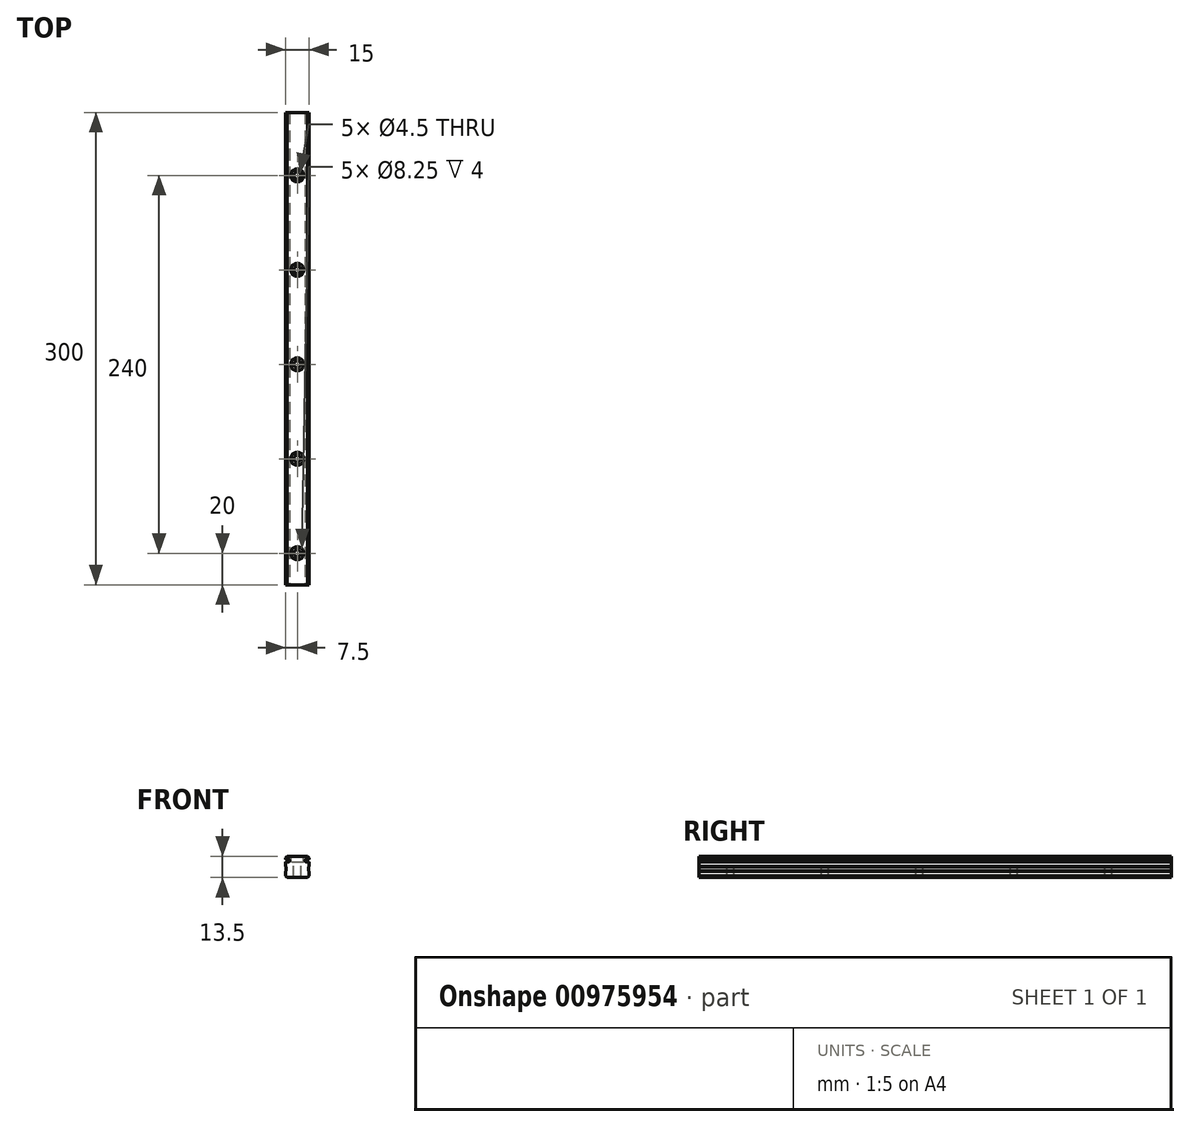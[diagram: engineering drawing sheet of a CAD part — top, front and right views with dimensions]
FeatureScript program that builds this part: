
annotation { "Feature Type Name" : "Feature", "Feature Type Description" : "" }
export const myFeature = defineFeature(function(context is Context, id is Id, definition is map)
    precondition{}
    {
        {
            var Q0;
            Q0=qCreatedBy(makeId("Front.planeOp"),FACE);
            var sketch = newSketch(context, id + "F0", { "sketchPlane" : qUnion([Q0])});
            skLineSegment(sketch, "E0.bottom", {"start": v(7.5, -6.75) * mm, "end": v(-7.5, -6.75) * mm});
            skLineSegment(sketch, "E0.top", {"start": v(7.5, 6.75) * mm, "end": v(-7.5, 6.75) * mm});
            skLineSegment(sketch, "E0.left", {"start": v(7.5, 5.25) * mm, "end": v(7.5, 6.75) * mm});
            skLineSegment(sketch, "E0.right", {"start": v(-7.5, 5.25) * mm, "end": v(-7.5, 6.75) * mm});
            skPoint(sketch, "E0.middle", {"position": v(0, 0) * mm});
            skLineSegment(sketch, "E1", {"start": v(-6.5, 6.75) * mm, "end": v(-7.5, 5.75) * mm});
            skLineSegment(sketch, "E2.MirrorCS", {"start": v(6.5, 6.75) * mm, "end": v(7.5, 5.75) * mm});
            skLineSegment(sketch, "E3.MirrorCS", {"start": v(-6.5, -6.75) * mm, "end": v(-7.5, -5.75) * mm});
            skLineSegment(sketch, "E4.MirrorCS", {"start": v(6.5, -6.75) * mm, "end": v(7.5, -5.75) * mm});
            skLineSegment(sketch, "E5", {"start": v(7.2, 0.25) * mm, "end": v(7.2, -2.75) * mm});
            skLineSegment(sketch, "E6", {"start": v(7.2, -2.75) * mm, "end": v(7.5, -2.75) * mm});
            skLineSegment(sketch, "E7", {"start": v(7.2, 0.25) * mm, "end": v(7.5, 0.25) * mm});
            skLineSegment(sketch, "E8.MirrorCS", {"start": v(-7.2, -2.75) * mm, "end": v(-7.5, -2.75) * mm});
            skLineSegment(sketch, "E9.MirrorCS", {"start": v(-7.2, 0.25) * mm, "end": v(-7.5, 0.25) * mm});
            skLineSegment(sketch, "E10.MirrorCS", {"start": v(-7.2, 0.25) * mm, "end": v(-7.2, -2.75) * mm});
            skLineSegment(sketch, "E11", {"start": v(5, 4.25) * mm, "end": v(5, 3.75) * mm});
            skLineSegment(sketch, "E12", {"start": v(5.5, 4.75) * mm, "end": v(7, 4.75) * mm});
            skLineSegment(sketch, "E13", {"start": v(5.5, 3.25) * mm, "end": v(7, 3.25) * mm});
            skLineSegment(sketch, "E14.MirrorCS", {"start": v(-5, 4.25) * mm, "end": v(-5, 3.75) * mm});
            skLineSegment(sketch, "E15.MirrorCS", {"start": v(-5.5, 4.75) * mm, "end": v(-7, 4.75) * mm});
            skLineSegment(sketch, "E16.MirrorCS", {"start": v(-5.5, 3.25) * mm, "end": v(-7, 3.25) * mm});
            skPoint(sketch, "E17.newPointA", {"position": v(7.5, 4.75) * mm});
            skArc(sketch, "E17.filletArc", {"start": v(7, 4.75) * mm, "mid": v(7.35, 4.9) * mm, "end": v(7.5, 5.25) * mm});
            skLineSegment(sketch, "E18", {"start": v(7.5, 2.75) * mm, "end": v(7.5, -6.75) * mm});
            skPoint(sketch, "E19.visualSharp", {"position": v(7.5, 3.25) * mm});
            skArc(sketch, "E19.filletArc", {"start": v(7.5, 2.75) * mm, "mid": v(7.35, 3.1) * mm, "end": v(7, 3.25) * mm});
            skPoint(sketch, "E20.newPointB", {"position": v(-7.5, 4.75) * mm});
            skArc(sketch, "E20.filletArc", {"start": v(-7.5, 5.25) * mm, "mid": v(-7.35, 4.9) * mm, "end": v(-7, 4.75) * mm});
            skLineSegment(sketch, "E21", {"start": v(-7.5, 2.75) * mm, "end": v(-7.5, -6.75) * mm});
            skPoint(sketch, "E22.visualSharp", {"position": v(-7.5, 3.25) * mm});
            skArc(sketch, "E22.filletArc", {"start": v(-7, 3.25) * mm, "mid": v(-7.35, 3.1) * mm, "end": v(-7.5, 2.75) * mm});
            skLineSegment(sketch, "E23", {"start": v(7.5, 0.25) * mm, "end": v(7.2, -0.05) * mm});
            skLineSegment(sketch, "E24", {"start": v(7.5, -2.75) * mm, "end": v(7.2, -2.45) * mm});
            skLineSegment(sketch, "E25.MirrorCS", {"start": v(-7.5, 0.25) * mm, "end": v(-7.2, -0.05) * mm});
            skLineSegment(sketch, "E26.MirrorCS", {"start": v(-7.5, -2.75) * mm, "end": v(-7.2, -2.45) * mm});
            skPoint(sketch, "E27.visualSharp", {"position": v(5, 4.75) * mm});
            skArc(sketch, "E27.filletArc", {"start": v(5.5, 4.75) * mm, "mid": v(5.15, 4.6) * mm, "end": v(5, 4.25) * mm});
            skPoint(sketch, "E28.visualSharp", {"position": v(5, 3.25) * mm});
            skArc(sketch, "E28.filletArc", {"start": v(5, 3.75) * mm, "mid": v(5.15, 3.4) * mm, "end": v(5.5, 3.25) * mm});
            skPoint(sketch, "E29.visualSharp", {"position": v(-5, 4.75) * mm});
            skArc(sketch, "E29.filletArc", {"start": v(-5, 4.25) * mm, "mid": v(-5.15, 4.6) * mm, "end": v(-5.5, 4.75) * mm});
            skPoint(sketch, "E30.visualSharp", {"position": v(-5, 3.25) * mm});
            skArc(sketch, "E30.filletArc", {"start": v(-5.5, 3.25) * mm, "mid": v(-5.15, 3.4) * mm, "end": v(-5, 3.75) * mm});
            skSolve(sketch);
        }
        {
            var Q0;
            {var subQ0=sQuery(id+"F0.wireOp",EDGE,"E1");Q0=makeQuery(id+"F0.imprint","IMPRINT",FACE,{"disambiguationData":[TD([[makeQuery(id+"F0.imprint","IMPRINT",EDGE,{"derivedFrom":subQ0}),1.0]])]});}
            var Q1;
            {var subQ0=sQuery(id+"F0.wireOp",EDGE,"E9.MirrorCS");Q1=makeQuery(id+"F0.imprint","IMPRINT",FACE,{"disambiguationData":[TD([[makeQuery(id+"F0.imprint","IMPRINT",EDGE,{"derivedFrom":subQ0}),1.0]])]});}
            var Q2;
            {var subQ0=sQuery(id+"F0.wireOp",EDGE,"E8.MirrorCS");Q2=makeQuery(id+"F0.imprint","IMPRINT",FACE,{"disambiguationData":[TD([[makeQuery(id+"F0.imprint","IMPRINT",EDGE,{"derivedFrom":subQ0}),-1.0]])]});}
            var Q3;
            {var subQ0=sQuery(id+"F0.wireOp",EDGE,"E6");Q3=makeQuery(id+"F0.imprint","IMPRINT",FACE,{"disambiguationData":[TD([[makeQuery(id+"F0.imprint","IMPRINT",EDGE,{"derivedFrom":subQ0}),1.0]])]});}
            var Q4;
            {var subQ0=sQuery(id+"F0.wireOp",EDGE,"E7");Q4=makeQuery(id+"F0.imprint","IMPRINT",FACE,{"disambiguationData":[TD([[makeQuery(id+"F0.imprint","IMPRINT",EDGE,{"derivedFrom":subQ0}),-1.0]])]});}
            extrude(context, id + "F1", {"entities" : qUnion([Q0, Q1, Q2, Q3, Q4]), "oppositeDirection" : true, "depth" : 300 * mm, "offsetDistance" : 25 * mm});
        }
        {
            var Q0;
            Q0=makeQuery(id+"F1.opExtrude","SWEPT_FACE",FACE,{"disambiguationData":[OSD([sQuery(id+"F0.wireOp",EDGE,"E0.top")])]});
            var sketch = newSketch(context, id + "F2", { "sketchPlane" : qUnion([Q0])});
            skPoint(sketch, "E31", {"position": v(0, 20) * mm});
            skPoint(sketch, "E32.0.1.0", {"position": v(0, 80) * mm});
            skPoint(sketch, "E32.0.2.0", {"position": v(0, 140) * mm});
            skPoint(sketch, "E32.0.3.0", {"position": v(0, 200) * mm});
            skPoint(sketch, "E32.0.4.0", {"position": v(0, 260) * mm});
            skLineSegment(sketch, "E32.direction1", {"start": v(0, 20) * mm, "end": v(25, 20) * mm, "construction": true});
            skLineSegment(sketch, "E32.direction2", {"start": v(0, 20) * mm, "end": v(0, 80) * mm, "construction": true});
            skSolve(sketch);
        }
        {
            var Q0;
            Q0=sQuery(id+"F2.wireOp",VERTEX,"E31");
            var Q1;
            Q1=sQuery(id+"F2.wireOp",VERTEX,"E32.0.1.0");
            var Q2;
            Q2=sQuery(id+"F2.wireOp",VERTEX,"E32.0.2.0");
            var Q3;
            Q3=sQuery(id+"F2.wireOp",VERTEX,"E32.0.3.0");
            var Q4;
            Q4=sQuery(id+"F2.wireOp",VERTEX,"E32.0.4.0");
            var Q5;
            Q5=makeQuery(id+"F1.opExtrude","SWEPT_BODY",BODY,{"disambiguationData":[OSD([sQuery(id+"F0.wireOp",EDGE,"E0.bottom"),sQuery(id+"F0.wireOp",EDGE,"E0.top"),sQuery(id+"F0.wireOp",EDGE,"E0.left"),sQuery(id+"F0.wireOp",EDGE,"E0.right"),sQuery(id+"F0.wireOp",EDGE,"E1"),sQuery(id+"F0.wireOp",EDGE,"E2.MirrorCS"),sQuery(id+"F0.wireOp",EDGE,"E3.MirrorCS"),sQuery(id+"F0.wireOp",EDGE,"E4.MirrorCS"),sQuery(id+"F0.wireOp",EDGE,"E5"),sQuery(id+"F0.wireOp",EDGE,"E6"),sQuery(id+"F0.wireOp",EDGE,"E7"),sQuery(id+"F0.wireOp",EDGE,"E8.MirrorCS"),sQuery(id+"F0.wireOp",EDGE,"E9.MirrorCS"),sQuery(id+"F0.wireOp",EDGE,"E10.MirrorCS"),sQuery(id+"F0.wireOp",EDGE,"E11"),sQuery(id+"F0.wireOp",EDGE,"E12"),sQuery(id+"F0.wireOp",EDGE,"E13"),sQuery(id+"F0.wireOp",EDGE,"E14.MirrorCS"),sQuery(id+"F0.wireOp",EDGE,"E15.MirrorCS"),sQuery(id+"F0.wireOp",EDGE,"E16.MirrorCS"),sQuery(id+"F0.wireOp",EDGE,"E17.filletArc"),sQuery(id+"F0.wireOp",EDGE,"E18"),sQuery(id+"F0.wireOp",EDGE,"E19.filletArc"),sQuery(id+"F0.wireOp",EDGE,"E20.filletArc"),sQuery(id+"F0.wireOp",EDGE,"E21"),sQuery(id+"F0.wireOp",EDGE,"E22.filletArc")])]});
            hole(context, id + "F3", {"style" : HoleStyle.C_BORE, "endStyle" : HoleEndStyle.THROUGH, "standardTappedOrClearance" : lookupTablePath({ "fit" : "Normal", "standard" : "ISO", "size" : "M4", "type" : "Clearance" }), "standardBlindInLast" : lookupTablePath({ "fit" : "Normal", "standard" : "ISO", "engagement" : "75%", "pitch" : "0.7 mm", "size" : "M4", "type" : "Clearance & tapped" }), "holeDiameter" : 4.5 * mm, "cBoreDiameter" : 8.25 * mm, "cBoreDepth" : 4 * mm, "majorDiameter" : 5 * mm, "isTappedThrough" : true, "tappedDepth" : 10 * mm, "tapClearance" : 3, "locations" : qUnion([Q0, Q1, Q2, Q3, Q4]), "scope" : qUnion([Q5])});
        }
    });
